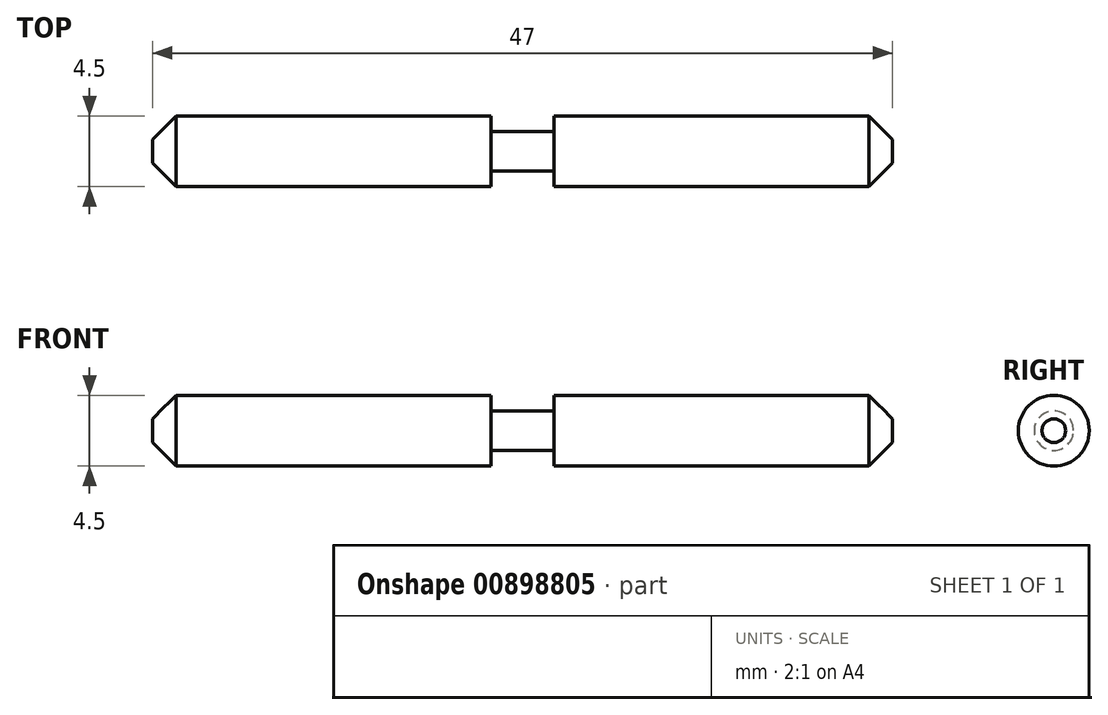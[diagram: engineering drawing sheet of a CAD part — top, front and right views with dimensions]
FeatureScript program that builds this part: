
annotation { "Feature Type Name" : "Feature", "Feature Type Description" : "" }
export const myFeature = defineFeature(function(context is Context, id is Id, definition is map)
    precondition{}
    {
        {
            var Q0;
            Q0=qCreatedBy(makeId("Top.planeOp"),FACE);
            var sketch = newSketch(context, id + "F0", { "sketchPlane" : qUnion([Q0])});
            skLineSegment(sketch, "E0.bottom", {"start": v(0, 0) * mm, "end": v(47, 0) * mm});
            skLineSegment(sketch, "E0.top", {"start": v(1.5, 2.25) * mm, "end": v(21.5, 2.25) * mm});
            skLineSegment(sketch, "E0.left", {"start": v(0, 0) * mm, "end": v(0, 0.75) * mm});
            skLineSegment(sketch, "E0.right", {"start": v(47, 0) * mm, "end": v(47, 0.75) * mm});
            skLineSegment(sketch, "E1", {"start": v(0, 0.75) * mm, "end": v(1.5, 2.25) * mm});
            skPoint(sketch, "E2.orphan", {"position": v(0, 2.25) * mm});
            skLineSegment(sketch, "E3.MirrorCS", {"start": v(47, 0.75) * mm, "end": v(45.5, 2.25) * mm});
            skLineSegment(sketch, "E4", {"start": v(21.5, 2.25) * mm, "end": v(21.5, 1.25) * mm});
            skLineSegment(sketch, "E5", {"start": v(25.5, 2.25) * mm, "end": v(25.5, 1.25) * mm});
            skLineSegment(sketch, "E6", {"start": v(21.5, 1.25) * mm, "end": v(25.5, 1.25) * mm});
            skPoint(sketch, "E7.orphan", {"position": v(23.5, 0) * mm});
            skLineSegment(sketch, "E8.trimOffspring", {"start": v(25.5, 2.25) * mm, "end": v(45.5, 2.25) * mm});
            skSolve(sketch);
        }
        {
            var Q0;
            Q0 = qSketchRegion(id + "F0", true);
            var Q1;
            Q1=sQuery(id+"F0.wireOp",EDGE,"E0.bottom");
            revolve(context, id + "F1", {"surfaceOperationType" : NewSurfaceOperationType.NEW, "entities" : qUnion([Q0]), "axis" : qUnion([Q1]), "revolveType" : RevolveType.FULL});
        }
    });
